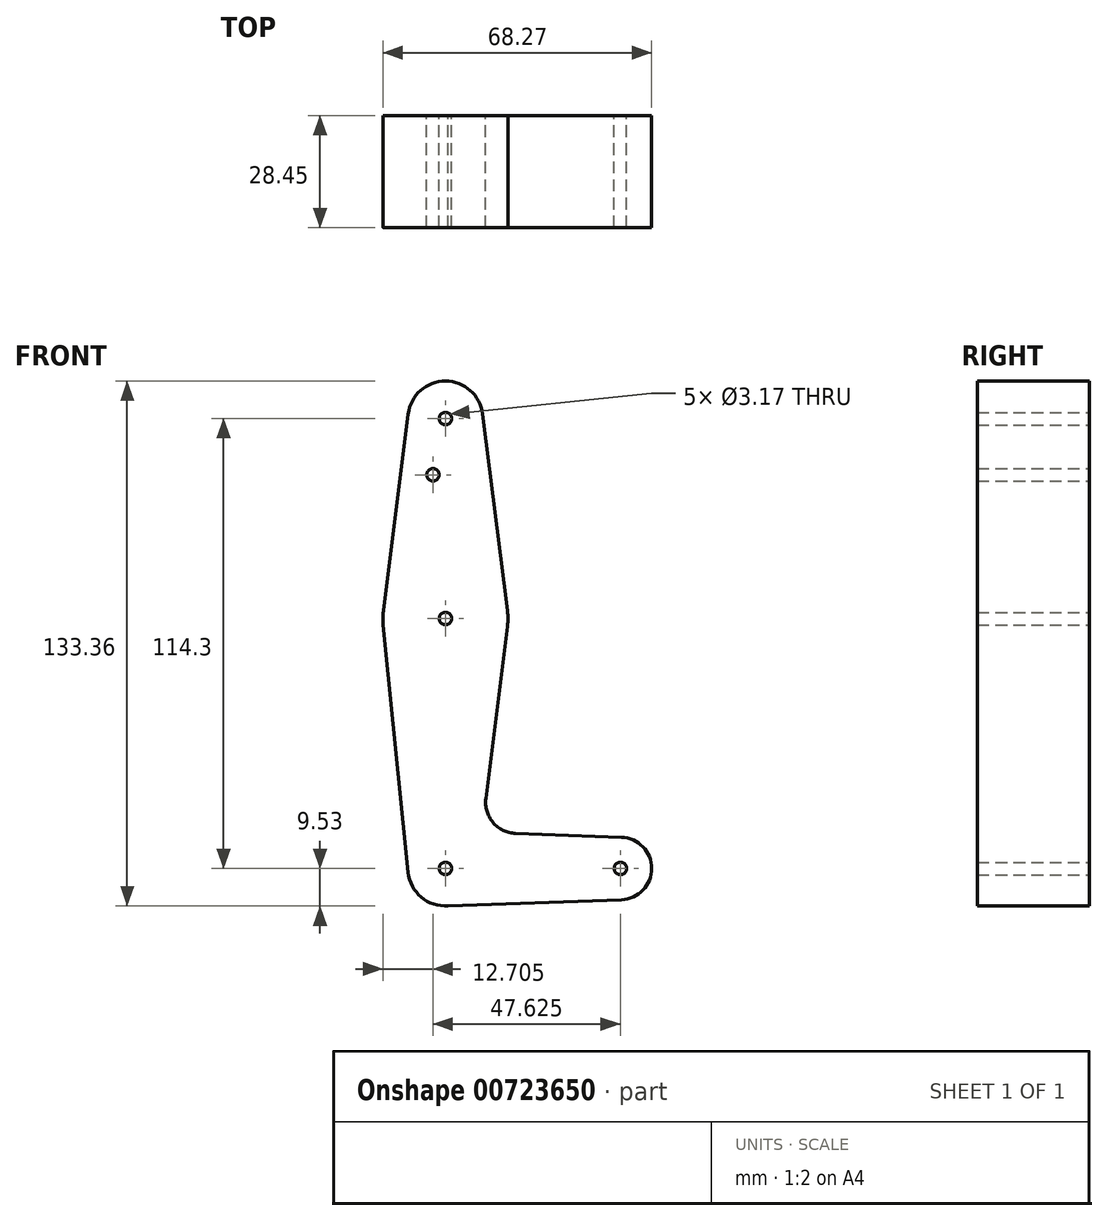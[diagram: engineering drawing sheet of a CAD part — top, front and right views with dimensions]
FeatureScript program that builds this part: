
annotation { "Feature Type Name" : "Feature", "Feature Type Description" : "" }
export const myFeature = defineFeature(function(context is Context, id is Id, definition is map)
    precondition{}
    {
        {
            var Q0;
            Q0=qCreatedBy(makeId("Front.planeOp"),FACE);
            var sketch = newSketch(context, id + "F0", { "sketchPlane" : qUnion([Q0])});
            skLineSegment(sketch, "E0", {"start": v(0, 114.3) * mm, "end": v(0, 0) * mm, "construction": true});
            skLineSegment(sketch, "E1", {"start": v(0, 0) * mm, "end": v(44.45, 0) * mm, "construction": true});
            skCircle(sketch, "E2", {"center": v(0, 114.3) * mm, "radius": 9.53 * mm});
            skCircle(sketch, "E3", {"center": v(0, 0) * mm, "radius": 9.53 * mm});
            skCircle(sketch, "E4", {"center": v(44.45, 0) * mm, "radius": 7.94 * mm});
            skCircle(sketch, "E5", {"center": v(0, 63.5) * mm, "radius": 15.88 * mm});
            skLineSegment(sketch, "E6", {"start": v(-9.45, 115.5) * mm, "end": v(-15.75, 65.48) * mm});
            skLineSegment(sketch, "E7", {"start": v(9.45, 115.5) * mm, "end": v(15.75, 65.48) * mm});
            skLineSegment(sketch, "E8", {"start": v(0, -9.52) * mm, "end": v(44.73, -7.93) * mm});
            skLineSegment(sketch, "E9", {"start": v(-15.8, 61.91) * mm, "end": v(-9.31, -2.6) * mm});
            skCircle(sketch, "E10", {"center": v(0, 114.3) * mm, "radius": 1.59 * mm});
            skCircle(sketch, "E11", {"center": v(0, 0) * mm, "radius": 1.59 * mm});
            skCircle(sketch, "E12", {"center": v(0, 63.5) * mm, "radius": 1.59 * mm});
            skCircle(sketch, "E13", {"center": v(44.45, 0) * mm, "radius": 1.59 * mm});
            skCircle(sketch, "E14", {"center": v(-3.17, 100.03) * mm, "radius": 1.59 * mm});
            skLineSegment(sketch, "E15", {"start": v(15.75, 61.52) * mm, "end": v(10.25, 17.83) * mm});
            skLineSegment(sketch, "E16", {"start": v(17.85, 8.9) * mm, "end": v(44.73, 7.93) * mm});
            skArc(sketch, "E17.filletArc", {"start": v(10.25, 17.83) * mm, "mid": v(12.08, 11.69) * mm, "end": v(17.85, 8.9) * mm});
            skSolve(sketch);
        }
        {
            var Q0;
            Q0 = qSketchRegion(id + "F0", true);
            extrude(context, id + "F1", {"entities" : qUnion([Q0]), "depth" : 28.45 * mm, "offsetDistance" : 25.4 * mm});
        }
    });
